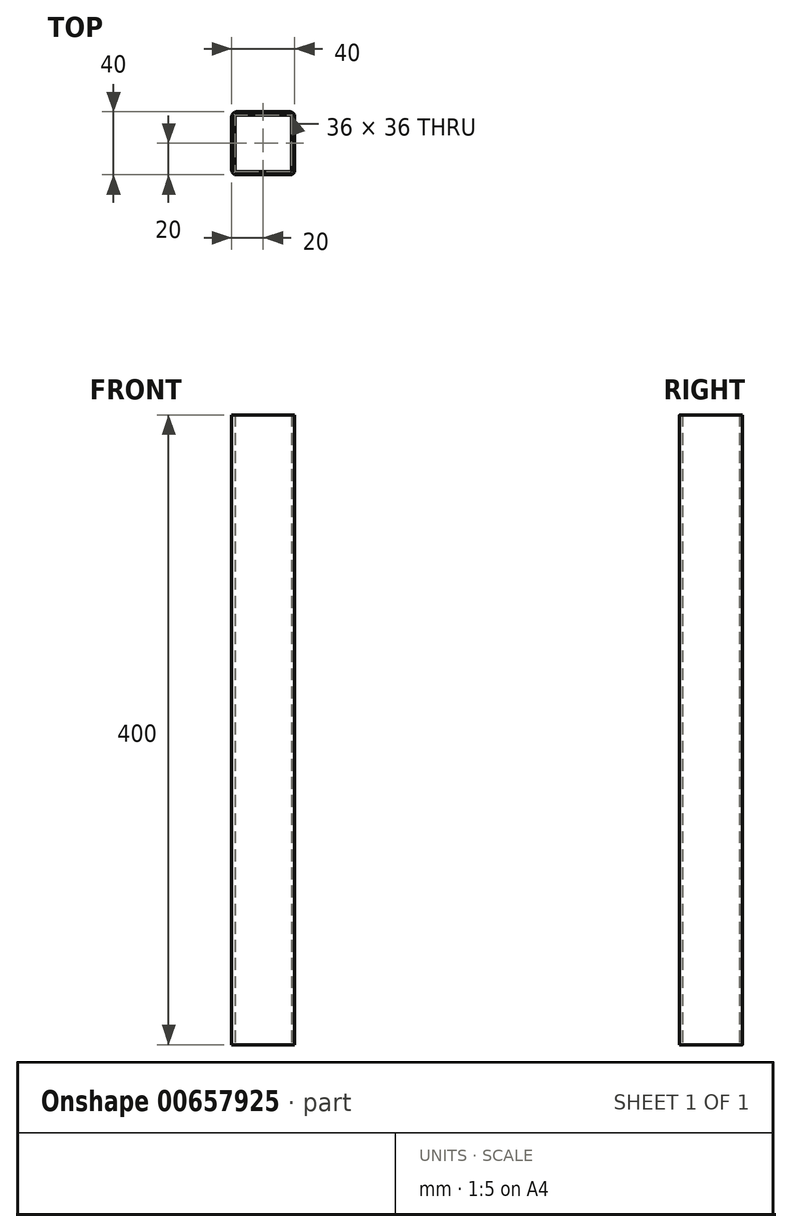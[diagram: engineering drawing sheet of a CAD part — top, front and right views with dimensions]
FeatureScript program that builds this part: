
annotation { "Feature Type Name" : "Feature", "Feature Type Description" : "" }
export const myFeature = defineFeature(function(context is Context, id is Id, definition is map)
    precondition{}
    {
        {
            var Q0;
            Q0=qCreatedBy(makeId("Top.planeOp"),FACE);
            var sketch = newSketch(context, id + "F0", { "sketchPlane" : qUnion([Q0])});
            skLineSegment(sketch, "E0.bottom", {"start": v(-17, 20) * mm, "end": v(17, 20) * mm});
            skLineSegment(sketch, "E0.top", {"start": v(-17, -20) * mm, "end": v(17, -20) * mm});
            skLineSegment(sketch, "E0.left", {"start": v(-20, 17) * mm, "end": v(-20, -17) * mm});
            skLineSegment(sketch, "E0.right", {"start": v(20, 17) * mm, "end": v(20, -17) * mm});
            skPoint(sketch, "E0.middle", {"position": v(0, 0) * mm});
            skPoint(sketch, "E1.visualSharp", {"position": v(-20, 20) * mm});
            skArc(sketch, "E1.filletArc", {"start": v(-17, 20) * mm, "mid": v(-19.12, 19.12) * mm, "end": v(-20, 17) * mm});
            skPoint(sketch, "E2.visualSharp", {"position": v(20, 20) * mm});
            skArc(sketch, "E2.filletArc", {"start": v(20, 17) * mm, "mid": v(19.12, 19.12) * mm, "end": v(17, 20) * mm});
            skPoint(sketch, "E3.visualSharp", {"position": v(20, -20) * mm});
            skArc(sketch, "E3.filletArc", {"start": v(17, -20) * mm, "mid": v(19.12, -19.12) * mm, "end": v(20, -17) * mm});
            skPoint(sketch, "E4.visualSharp", {"position": v(-20, -20) * mm});
            skArc(sketch, "E4.filletArc", {"start": v(-20, -17) * mm, "mid": v(-19.12, -19.12) * mm, "end": v(-17, -20) * mm});
            skLineSegment(sketch, "E5.0", {"start": v(-18, 18) * mm, "end": v(-18, -18) * mm});
            skLineSegment(sketch, "E5.1", {"start": v(-18, 18) * mm, "end": v(18, 18) * mm});
            skLineSegment(sketch, "E5.2", {"start": v(18, 18) * mm, "end": v(18, -18) * mm});
            skLineSegment(sketch, "E5.3", {"start": v(-18, -18) * mm, "end": v(18, -18) * mm});
            skSolve(sketch);
        }
        {
            var Q0;
            Q0=makeQuery(id+"F0.imprint","IMPRINT",FACE,{"disambiguationData":[TD([[makeQuery(id+"F0.imprint","IMPRINT",EDGE,{"derivedFrom":sQuery(id+"F0.wireOp",EDGE,"E0.bottom")}),-1.0]])]});
            extrude(context, id + "F1", {"entities" : qUnion([Q0]), "depth" : 400 * mm, "offsetDistance" : 25 * mm});
        }
    });
